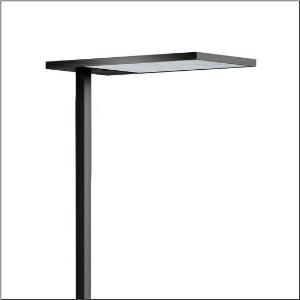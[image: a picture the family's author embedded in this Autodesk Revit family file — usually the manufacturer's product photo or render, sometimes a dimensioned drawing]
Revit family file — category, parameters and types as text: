
# Revit family: silica_21_floor_r_51mx53sg4db
name_source: partatom
category: Lighting Fixtures
units: mm (PartAtom-declared; Revit-internal decimal feet)

## family parameters
Cut with Voids When Loaded = No
Host = Face
Light Source = No
Part Type = Normal
Room Calculation Point = No
Round Connector Dimension = Use Diameter
Shared = No

## types (1)
- Silica 21 Floor R (1 x LED, 15000 lm, 106.4 W, 4000K)
    Apparent Load = 106 VA
    CIE Flux Codes = 54 86 97 13 100
    Color Rendering = 80
    Color Temperature = 4000K
    Default Elevation = 1800 mm
    Description = Silica® 21 Floor R, floorstanding luminaire, of PMMA, primary optical cover: prismatic diffuser, of PMMA, CAT 2 (L<= 3000cd/m²), light emission: indirect/direct distribution, primary light characteristic: symmetric, primary optical cover: cover panel, of PMMA, installation type: not mounted, LED, rated luminous flux: 15.000lm, luminous efficacy: 141lm/W, light colour: 840, colour temperature: 4000K, control gear: DALI 2, daylight-dependent control, mains connection: 230V, AC, 50/60Hz, connection cable included, cable length: 2,5m, rated input power: 106.4W, luminaire head, of aluminium, powder-coated, jet black (RAL 9005), length: 671mm, width: 371mm, height: 2010mm, supporting column, angular, of aluminium, powder-coated, jet black (RAL 9005), baseplate, of steel, powder-coated, jet black (RAL 9005), sensor module PR3-S, local control - self-sufficient standalone sensors, equipment: master, dimmable, protection rating (complete): IP20, insulation class (complete): insulation class I (protective earthing), certification: CE, permissible operating ambient temperature: 0..+35°C, standard: EN 50419, packaging unit: 1 piece
    Height = 18 mm
    Lamp = 1 x LED
    Lamp Light Flux = 15000 lm
    Lamp Power = 106.4 W
    Lamp count = 1
    Length = 650 mm
    Luminous efficacy = 141 lm/W
    Manufacturer = Siteco
    ModVariant = No
    Model = 51MX53SG4DB
    Mounting Place = Floor
    Mounting Type = Freestanding
    Number of Poles = 1
    OnlyDefault = Yes
    Power Factor = 1
    Product Name = Silica 21 Floor R
    Product group = floorstanding luminaire
    ProductGroupID = 1302
    Protection Class = Protection class I
    Protection Degree = IP 20
    RLX_Detail_Level = 1
    RLX_Emergency_Light_Flux = 0 lm
    RLX_Emergency_Type = 0
    RLX_Emergency_Type_DB = No
    RlxData = <blob elided: 22185 chars, md5=b953c577>
    Socket = socket
    Standby Power = 0 W
    System Light Flux = 15000 lm
    System Power = 106 W
    Type Comments = Product without accessories
    Type Image = l_1007011.jpg
    URL = http://relux.com
    VarID = ---
    Voltage = 0 V
    Weight = 0.00 kg
    Width = 350 mm

## geometry (parser evidence)
native form markers: Blend x4, Sweep x17
no freeform markers — native parametric forms only
